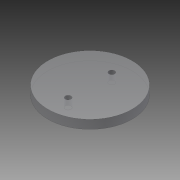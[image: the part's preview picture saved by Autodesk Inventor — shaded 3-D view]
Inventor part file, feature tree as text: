
AUTODESK INVENTOR PART (.ipt)
format: ipt  version: 2015 (Build 190159000, 159)  size: 91,648 bytes
history: native  units: mm
features: extrude x2, sketch x2
ambient origin geometry x8: Origin, YZ Plane, XZ Plane, XY Plane, X Axis, Y Axis, Z Axis, Center Point
bodies: Solid1 (feature_tree)
feature tree (4):
  extrude  "Extrusion1"  Depth=3.0mm TaperAngle=0.0deg
  extrude  "Extrusion4"  Depth=10.0mm
  sketch  "Sketch1"  dims[d0=28.85mm d3=3.0mm d4=0.0mm]
  sketch  "Sketch2"  dims[d22=9.5mm d31=2.0mm d34=15.0mm d35=7.5mm d36=10.0mm d37=0.0mm]
